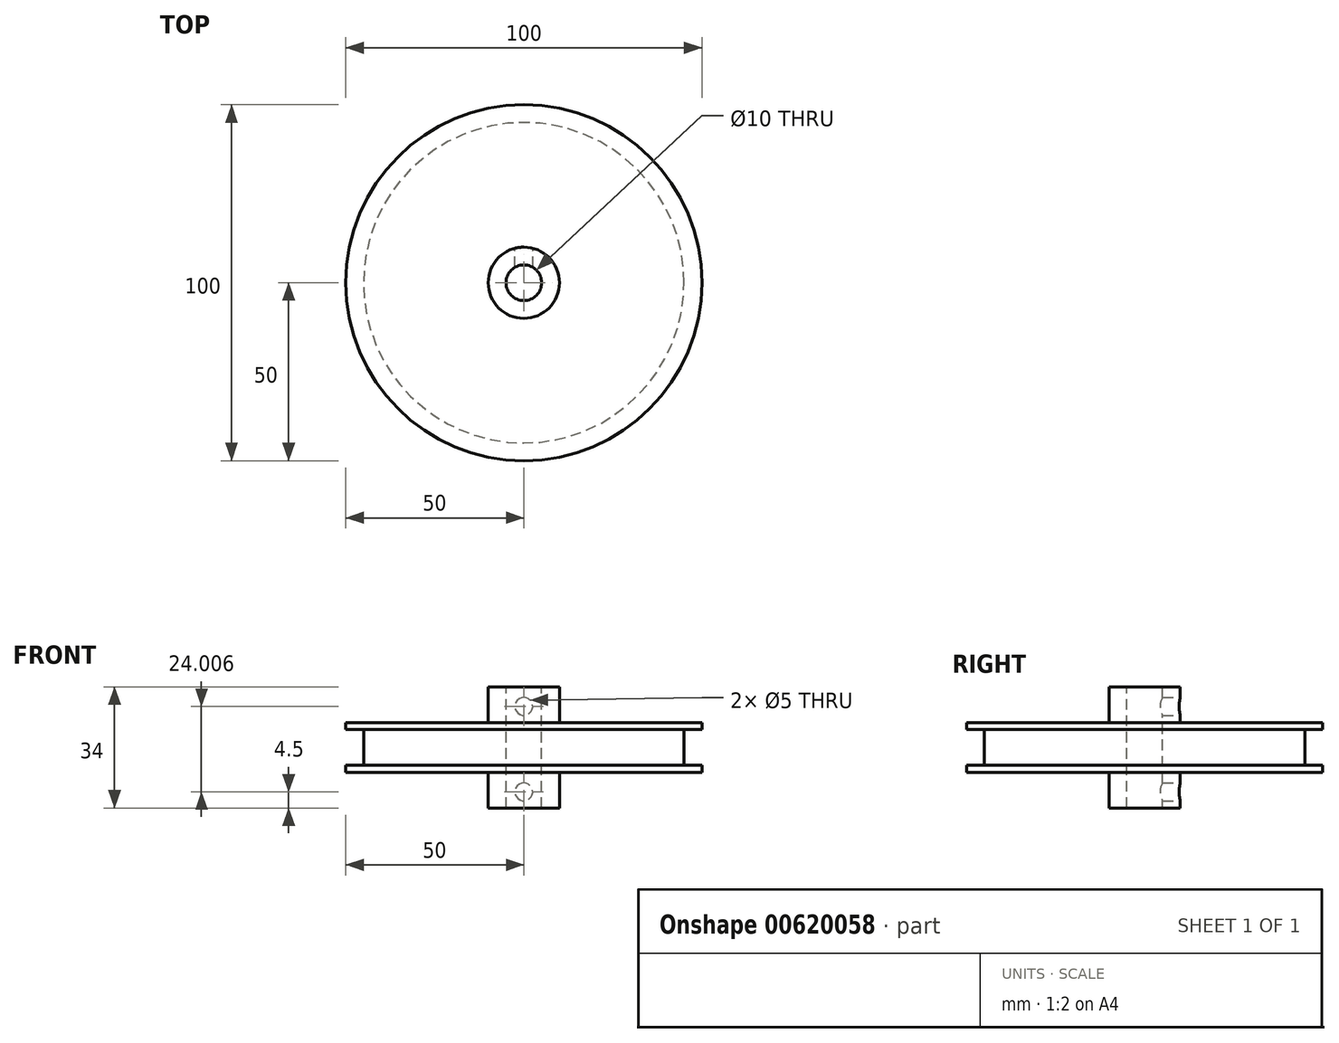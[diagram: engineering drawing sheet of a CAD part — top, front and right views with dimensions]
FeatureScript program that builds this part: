
annotation { "Feature Type Name" : "Feature", "Feature Type Description" : "" }
export const myFeature = defineFeature(function(context is Context, id is Id, definition is map)
    precondition{}
    {
        {
            var Q0;
            Q0=qCreatedBy(makeId("Top.planeOp"),FACE);
            var sketch = newSketch(context, id + "F0", { "sketchPlane" : qUnion([Q0])});
            skCircle(sketch, "E0", {"center": v(0, 0) * mm, "radius": 50 * mm});
            skSolve(sketch);
        }
        {
            var Q0;
            Q0=makeQuery(id+"F0.imprint","IMPRINT",FACE,{"disambiguationData":[TD([[makeQuery(id+"F0.imprint","IMPRINT",EDGE,{"derivedFrom":sQuery(id+"F0.wireOp",EDGE,"E0")}),1.0]])]});
            extrude(context, id + "F1", {"entities" : qUnion([Q0]), "depth" : 2 * mm, "offsetDistance" : 25 * mm});
        }
        {
            var Q0;
            Q0=makeQuery(id+"F1.opExtrude","CAP_FACE",FACE,{"disambiguationData":[OSD([sQuery(id+"F0.wireOp",EDGE,"E0")])],"isStart":false});
            var sketch = newSketch(context, id + "F2", { "sketchPlane" : qUnion([Q0])});
            skCircle(sketch, "E1", {"center": v(0, 0) * mm, "radius": 45 * mm});
            skSolve(sketch);
        }
        {
            var Q0;
            Q0 = qSketchRegion(id + "F2", true);
            extrude(context, id + "F3", {"entities" : qUnion([Q0]), "operationType" : NewBodyOperationType.ADD, "depth" : 10 * mm, "offsetDistance" : 25 * mm});
        }
        {
            var Q0;
            Q0=makeQuery(id+"F3.opExtrude","CAP_FACE",FACE,{"disambiguationData":[OSD([sQuery(id+"F2.wireOp",EDGE,"E1")])],"isStart":false});
            var sketch = newSketch(context, id + "F4", { "sketchPlane" : qUnion([Q0])});
            skCircle(sketch, "E2", {"center": v(0, 0) * mm, "radius": 50 * mm});
            skSolve(sketch);
        }
        {
            var Q0;
            Q0=makeQuery(id+"F4.imprint","IMPRINT",FACE,{"disambiguationData":[TD([[makeQuery(id+"F4.imprint","IMPRINT",EDGE,{"derivedFrom":makeQuery(id+"F3.opExtrude","CAP_EDGE",EDGE,{"disambiguationData":[OSD([sQuery(id+"F2.wireOp",EDGE,"E1")])],"isStart":false})}),1.0]])]});
            var Q1;
            Q1=makeQuery(id+"F4.imprint","IMPRINT",FACE,{"disambiguationData":[TD([[makeQuery(id+"F4.imprint","IMPRINT",EDGE,{"derivedFrom":sQuery(id+"F4.wireOp",EDGE,"E2")}),1.0]])]});
            extrude(context, id + "F5", {"entities" : qUnion([Q0, Q1]), "operationType" : NewBodyOperationType.ADD, "depth" : 2 * mm, "offsetDistance" : 25 * mm});
        }
        {
            var Q0;
            Q0=makeQuery(id+"F5.opExtrude","CAP_FACE",FACE,{"disambiguationData":[OSD([sQuery(id+"F4.wireOp",EDGE,"E2")])],"isStart":false});
            var sketch = newSketch(context, id + "F6", { "sketchPlane" : qUnion([Q0])});
            skCircle(sketch, "E3", {"center": v(0, 0) * mm, "radius": 10 * mm});
            skSolve(sketch);
        }
        {
            var Q0;
            Q0=makeQuery(id+"F6.imprint","IMPRINT",FACE,{"disambiguationData":[TD([[makeQuery(id+"F6.imprint","IMPRINT",EDGE,{"derivedFrom":sQuery(id+"F6.wireOp",EDGE,"E3")}),1.0]])]});
            extrude(context, id + "F7", {"entities" : qUnion([Q0]), "operationType" : NewBodyOperationType.ADD, "depth" : 10 * mm, "offsetDistance" : 25 * mm});
        }
        {
            var Q0;
            Q0=makeQuery(id+"F1.opExtrude","CAP_FACE",FACE,{"disambiguationData":[OSD([sQuery(id+"F0.wireOp",EDGE,"E0")])],"isStart":true});
            var sketch = newSketch(context, id + "F8", { "sketchPlane" : qUnion([Q0])});
            skCircle(sketch, "E4", {"center": v(0, 0) * mm, "radius": 10 * mm});
            skSolve(sketch);
        }
        {
            var Q0;
            Q0=makeQuery(id+"F8.imprint","IMPRINT",FACE,{"disambiguationData":[TD([[makeQuery(id+"F8.imprint","IMPRINT",EDGE,{"derivedFrom":sQuery(id+"F8.wireOp",EDGE,"E4")}),1.0]])]});
            extrude(context, id + "F9", {"entities" : qUnion([Q0]), "operationType" : NewBodyOperationType.ADD, "depth" : 10 * mm, "offsetDistance" : 25 * mm});
        }
        {
            var Q0;
            Q0=makeQuery(id+"F7.opExtrude","CAP_FACE",FACE,{"disambiguationData":[OSD([sQuery(id+"F6.wireOp",EDGE,"E3")])],"isStart":false});
            var sketch = newSketch(context, id + "F10", { "sketchPlane" : qUnion([Q0])});
            skCircle(sketch, "E5", {"center": v(0, 0) * mm, "radius": 5 * mm});
            skSolve(sketch);
        }
        {
            var Q0;
            Q0=makeQuery(id+"F10.imprint","IMPRINT",FACE,{"disambiguationData":[TD([[makeQuery(id+"F10.imprint","IMPRINT",EDGE,{"derivedFrom":sQuery(id+"F10.wireOp",EDGE,"E5")}),1.0]])]});
            extrude(context, id + "F11", {"entities" : qUnion([Q0]), "operationType" : NewBodyOperationType.REMOVE, "endBound" : BoundingType.THROUGH_ALL, "oppositeDirection" : true, "depth" : 25 * mm, "offsetDistance" : 25 * mm});
        }
        {
            var Q0;
            Q0=makeQuery(id+"F7.opExtrude","CAP_FACE",FACE,{"disambiguationData":[OSD([sQuery(id+"F6.wireOp",EDGE,"E3")])],"isStart":false});
            var sketch = newSketch(context, id + "F12", { "sketchPlane" : qUnion([Q0])});
            skLineSegment(sketch, "E6", {"start": v(-26.54, 10) * mm, "end": v(26.01, 10) * mm});
            skSolve(sketch);
        }
        {
            var Q0;
            Q0=sQuery(id+"F12.wireOp",EDGE,"E6");
            extrude(context, id + "F13", {"bodyType" : ToolBodyType.SURFACE, "surfaceEntities" : qUnion([Q0]), "oppositeDirection" : true, "depth" : 40 * mm, "offsetDistance" : 25 * mm});
        }
        {
            var Q0;
            Q0=makeQuery(id+"F13.opExtrude","SWEPT_FACE",FACE,{"disambiguationData":[OSD([sQuery(id+"F12.wireOp",EDGE,"E6")])]});
            var sketch = newSketch(context, id + "F14", { "sketchPlane" : qUnion([Q0])});
            skCircle(sketch, "E7", {"center": v(0, 18.5) * mm, "radius": 2.5 * mm});
            skCircle(sketch, "E8", {"center": v(0, -5.5) * mm, "radius": 2.5 * mm});
            skSolve(sketch);
        }
        {
            var Q0;
            Q0=makeQuery(id+"F14.imprint","IMPRINT",FACE,{"disambiguationData":[TD([[makeQuery(id+"F14.imprint","IMPRINT",EDGE,{"derivedFrom":sQuery(id+"F14.wireOp",EDGE,"E7")}),1.0]])]});
            var Q1;
            Q1=makeQuery(id+"F14.imprint","IMPRINT",FACE,{"disambiguationData":[TD([[makeQuery(id+"F14.imprint","IMPRINT",EDGE,{"derivedFrom":sQuery(id+"F14.wireOp",EDGE,"E8")}),1.0]])]});
            var Q2;
            Q2=makeQuery(id+"F11.boolean.opBoolean","COPY",FACE,{"derivedFrom":makeQuery(id+"F11.opExtrude","SWEPT_FACE",FACE,{"disambiguationData":[OSD([sQuery(id+"F10.wireOp",EDGE,"E5")])]})});
            extrude(context, id + "F15", {"entities" : qUnion([Q0, Q1]), "operationType" : NewBodyOperationType.REMOVE, "endBound" : BoundingType.UP_TO_SURFACE, "oppositeDirection" : true, "depth" : 25 * mm, "endBoundEntityFace" : qUnion([Q2]), "offsetDistance" : 25 * mm});
        }
    });
